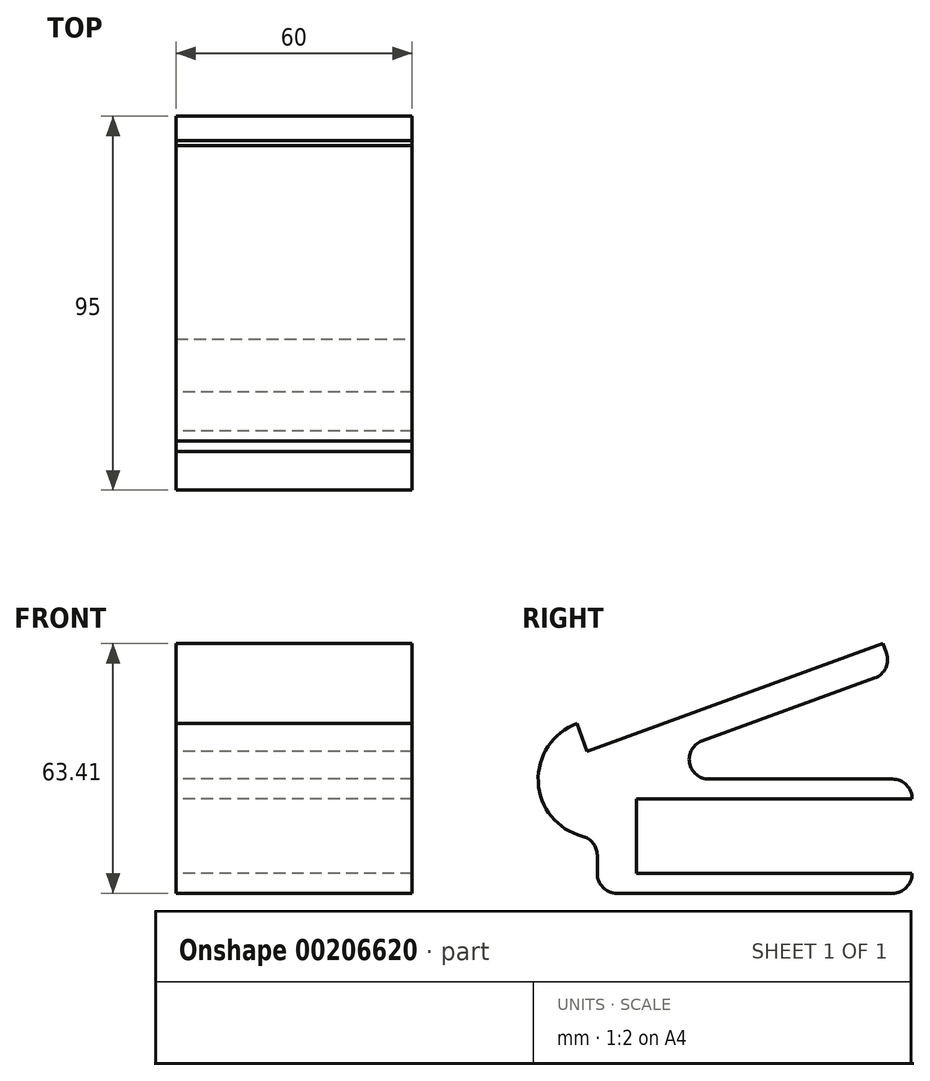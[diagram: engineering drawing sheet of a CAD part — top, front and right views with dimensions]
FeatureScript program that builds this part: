
annotation { "Feature Type Name" : "Feature", "Feature Type Description" : "" }
export const myFeature = defineFeature(function(context is Context, id is Id, definition is map)
    precondition{}
    {
        {
            var Q0;
            Q0=qCreatedBy(makeId("Right.planeOp"),FACE);
            var sketch = newSketch(context, id + "F0", { "sketchPlane" : qUnion([Q0])});
            skLineSegment(sketch, "E0.bottom", {"start": v(0, 0) * mm, "end": v(-80, 0) * mm});
            skLineSegment(sketch, "E0.top", {"start": v(0, 29) * mm, "end": v(-80, 29) * mm});
            skLineSegment(sketch, "E0.left", {"start": v(0, 0) * mm, "end": v(0, 29) * mm});
            skLineSegment(sketch, "E0.right", {"start": v(-80, 0) * mm, "end": v(-80, 29) * mm});
            skPoint(sketch, "E1", {"position": v(0, 14.5) * mm});
            skLineSegment(sketch, "E2.bottom", {"start": v(-70, 5) * mm, "end": v(70, 5) * mm});
            skLineSegment(sketch, "E2.top", {"start": v(-70, 24) * mm, "end": v(70, 24) * mm});
            skLineSegment(sketch, "E2.left", {"start": v(-70, 5) * mm, "end": v(-70, 24) * mm});
            skLineSegment(sketch, "E2.right", {"start": v(70, 5) * mm, "end": v(70, 24) * mm});
            skLineSegment(sketch, "E3", {"start": v(-80, 29) * mm, "end": v(-4.82, 56.36) * mm});
            skLineSegment(sketch, "E4", {"start": v(-4.82, 56.36) * mm, "end": v(-7.39, 63.4) * mm});
            skLineSegment(sketch, "E5", {"start": v(-80, 29) * mm, "end": v(-82.57, 36.05) * mm});
            skLineSegment(sketch, "E6", {"start": v(-82.57, 36.05) * mm, "end": v(-7.39, 63.4) * mm});
            skLineSegment(sketch, "E7", {"start": v(-82.57, 36.05) * mm, "end": v(-85.13, 43.1) * mm});
            skArc(sketch, "E8", {"start": v(-85.13, 43.1) * mm, "mid": v(-94.77, 26.4) * mm, "end": v(-80, 14) * mm});
            skSolve(sketch);
        }
        {
            var Q0;
            {var subQ4=sQuery(id+"F0.wireOp",EDGE,"E0.bottom");Q0=makeQuery(id+"F0.imprint","IMPRINT",FACE,{"disambiguationData":[TD([[makeQuery(id+"F0.imprint","IMPRINT",EDGE,{"derivedFrom":subQ4}),-1.0]])]});}
            var Q1;
            {var subQ0=sQuery(id+"F0.wireOp",EDGE,"E5");Q1=makeQuery(id+"F0.imprint","IMPRINT",FACE,{"disambiguationData":[TD([[makeQuery(id+"F0.imprint","IMPRINT",EDGE,{"derivedFrom":subQ0}),1.0]])]});}
            var Q2;
            Q2=makeQuery(id+"F0.imprint","IMPRINT",FACE,{"disambiguationData":[TD([[makeQuery(id+"F0.imprint","IMPRINT",EDGE,{"derivedFrom":sQuery(id+"F0.wireOp",EDGE,"E3")}),1.0]])]});
            extrude(context, id + "F1", {"entities" : qUnion([Q0, Q1, Q2]), "depth" : 60 * mm});
        }
        {
            var Q0;
            Q0=makeQuery(id+"F1.opExtrude","SWEPT_EDGE",EDGE,{"disambiguationData":[OSD([sQuery(id+"F0.wireOp",EDGE,"E0.top"),sQuery(id+"F0.wireOp",EDGE,"E0.right"),sQuery(id+"F0.wireOp",EDGE,"E3"),sQuery(id+"F0.wireOp",EDGE,"E5")])]});
            var Q1;
            Q1=makeQuery(id+"F1.opExtrude","SWEPT_EDGE",EDGE,{"disambiguationData":[OSD([sQuery(id+"F0.wireOp",EDGE,"E0.right"),sQuery(id+"F0.wireOp",EDGE,"E8")])]});
            var Q2;
            Q2=makeQuery(id+"F1.opExtrude","SWEPT_EDGE",EDGE,{"disambiguationData":[OSD([sQuery(id+"F0.wireOp",EDGE,"E0.bottom"),sQuery(id+"F0.wireOp",EDGE,"E0.right")])]});
            var Q3;
            Q3=makeQuery(id+"F1.opExtrude","SWEPT_EDGE",EDGE,{"disambiguationData":[OSD([sQuery(id+"F0.wireOp",EDGE,"E0.bottom"),sQuery(id+"F0.wireOp",EDGE,"E0.left")])]});
            var Q4;
            Q4=makeQuery(id+"F1.opExtrude","SWEPT_EDGE",EDGE,{"disambiguationData":[OSD([sQuery(id+"F0.wireOp",EDGE,"E0.top"),sQuery(id+"F0.wireOp",EDGE,"E0.left")])]});
            var Q5;
            Q5=makeQuery(id+"F1.opExtrude","SWEPT_EDGE",EDGE,{"disambiguationData":[OSD([sQuery(id+"F0.wireOp",EDGE,"E3"),sQuery(id+"F0.wireOp",EDGE,"E4")])]});
            fillet(context, id + "F2", {"entities" : qUnion([Q0, Q1, Q2, Q3, Q4, Q5]), "radius" : 5 * mm, "tangentPropagation" : true, "allowEdgeOverflow" : false});
        }
    });
